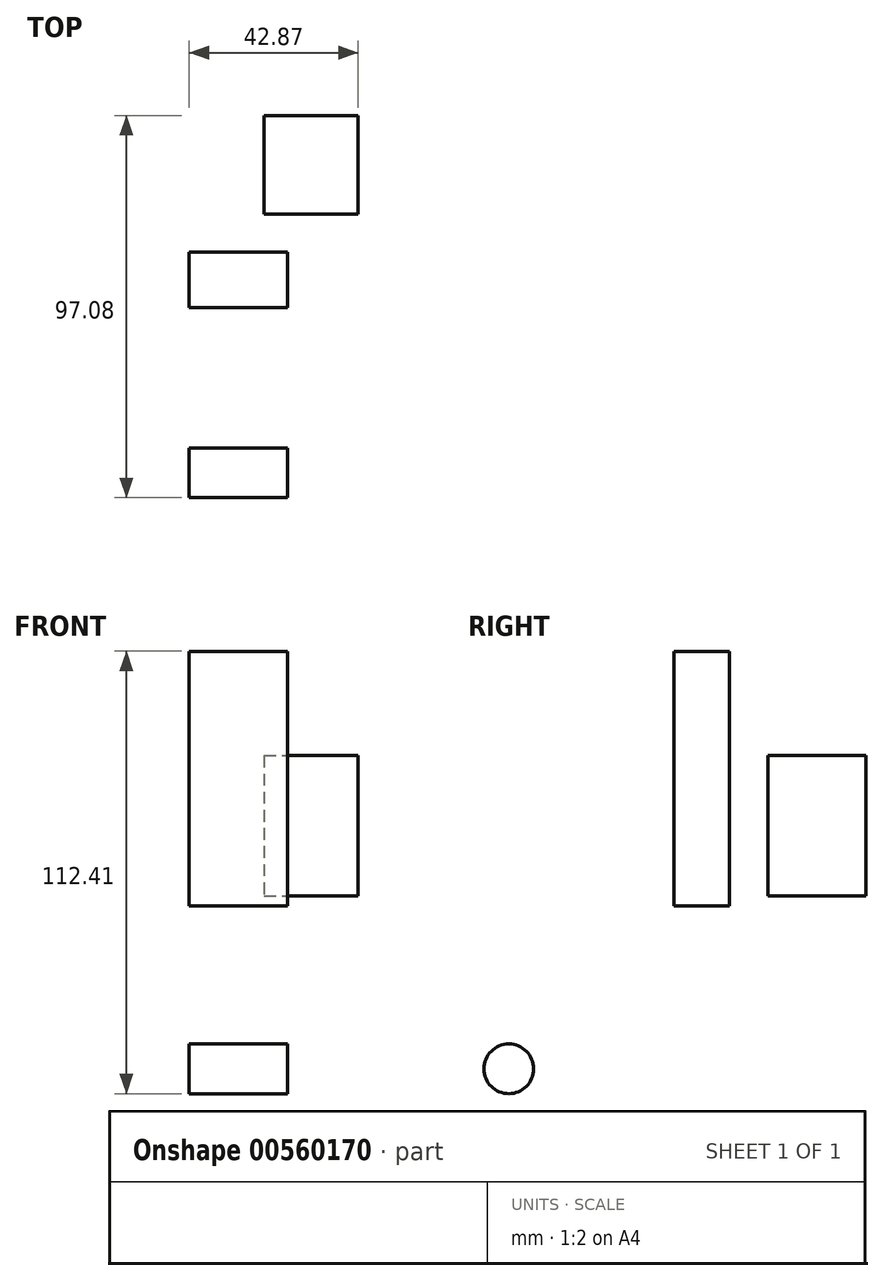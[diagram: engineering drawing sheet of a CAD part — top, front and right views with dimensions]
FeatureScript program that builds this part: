
annotation { "Feature Type Name" : "Feature", "Feature Type Description" : "" }
export const myFeature = defineFeature(function(context is Context, id is Id, definition is map)
    precondition{}
    {
        {
            var Q0;
            Q0=qCreatedBy(makeId("Front.planeOp"),FACE);
            var sketch = newSketch(context, id + "F0", { "sketchPlane" : qUnion([Q0])});
            skLineSegment(sketch, "E0.bottom", {"start": v(-34.62, 46.58) * mm, "end": v(-10.73, 46.58) * mm});
            skLineSegment(sketch, "E0.top", {"start": v(-34.62, 10.94) * mm, "end": v(-10.73, 10.94) * mm});
            skLineSegment(sketch, "E0.left", {"start": v(-34.62, 46.58) * mm, "end": v(-34.62, 10.94) * mm});
            skLineSegment(sketch, "E0.right", {"start": v(-10.73, 46.58) * mm, "end": v(-10.73, 10.94) * mm});
            skSolve(sketch);
        }
        {
            var Q0;
            Q0 = qSketchRegion(id + "F0", true);
            extrude(context, id + "F1", {"entities" : qUnion([Q0]), "depth" : 25 * mm, "offsetDistance" : 25 * mm});
        }
        {
            var Q0;
            Q0=makeQuery(id+"F1.opExtrude","SWEPT_BODY",BODY,{"disambiguationData":[OSD([sQuery(id+"F0.wireOp",EDGE,"E0.bottom"),sQuery(id+"F0.wireOp",EDGE,"E0.top"),sQuery(id+"F0.wireOp",EDGE,"E0.left"),sQuery(id+"F0.wireOp",EDGE,"E0.right")])]});
            var Q1;
            Q1=makeQuery(id+"F1.opExtrude","CAP_EDGE",EDGE,{"disambiguationData":[OSD([sQuery(id+"F0.wireOp",EDGE,"E0.bottom")])],"isStart":false});
            var Q2;
            Q2=makeQuery(id+"F1.opExtrude","CAP_EDGE",EDGE,{"disambiguationData":[OSD([sQuery(id+"F0.wireOp",EDGE,"E0.bottom")])],"isStart":false});
            transform(context, id + "F2", {"entities" : qUnion([Q0]), "transformType" : TransformType.TRANSLATION_DISTANCE, "transformDirection" : qUnion([Q2]), "distance" : 53.6 * mm, "makeCopy" : false});
        }
        {
            var Q0;
            Q0=qCreatedBy(makeId("Right.planeOp"),FACE);
            var sketch = newSketch(context, id + "F3", { "sketchPlane" : qUnion([Q0])});
            skLineSegment(sketch, "E1.bottom", {"start": v(-48.76, 8.36) * mm, "end": v(-34.7, 8.36) * mm});
            skLineSegment(sketch, "E1.top", {"start": v(-48.76, 73.1) * mm, "end": v(-34.7, 73.1) * mm});
            skLineSegment(sketch, "E1.left", {"start": v(-48.76, 8.36) * mm, "end": v(-48.76, 73.1) * mm});
            skLineSegment(sketch, "E1.right", {"start": v(-34.7, 8.36) * mm, "end": v(-34.7, 73.1) * mm});
            skSolve(sketch);
        }
        {
            var Q0;
            Q0 = qSketchRegion(id + "F3", true);
            extrude(context, id + "F4", {"entities" : qUnion([Q0]), "depth" : 25 * mm, "offsetDistance" : 25 * mm});
        }
        {
            var Q0;
            Q0=qCreatedBy(makeId("Right.planeOp"),FACE);
            var sketch = newSketch(context, id + "F5", { "sketchPlane" : qUnion([Q0])});
            skCircle(sketch, "E2", {"center": v(-90.77, -33) * mm, "radius": 6.3 * mm});
            skSolve(sketch);
        }
        {
            var Q0;
            Q0 = qSketchRegion(id + "F5", true);
            extrude(context, id + "F6", {"entities" : qUnion([Q0]), "depth" : 25 * mm, "offsetDistance" : 25 * mm});
        }
    });
